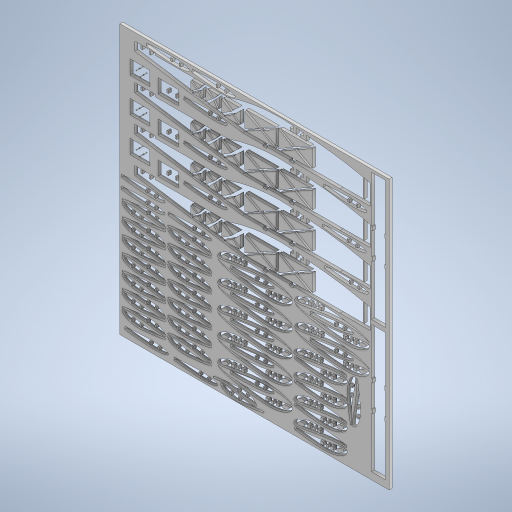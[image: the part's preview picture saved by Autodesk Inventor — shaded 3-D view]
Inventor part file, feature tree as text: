
AUTODESK INVENTOR PART (.ipt)
format: ipt  version: 2024 (Build 280153000, 153)  size: 2,372,096 bytes
history: native  units: in
note: dims shown in document units (in); Inventor stores cm internally (conversion verified against a paired STEP export)
features: extrude x13, sketch x13, pattern_linear x9
ambient origin geometry x8: Origin, YZ Plane, XZ Plane, XY Plane, X Axis, Y Axis, Z Axis, Center Point
bodies: Solid1 (feature_tree)
feature tree (35):
  extrude  "Extrusion1"  Depth=0.3937in TaperAngle=0.0deg
  extrude  "Extrusion6"  Depth=0.3937in TaperAngle=0.0deg
  pattern_linear  "Rectangular Pattern4"  Count1=3 Spacing1=4.685in
  extrude  "Extrusion7"  Depth=6.0236in
  pattern_linear  "Rectangular Pattern5"  Count1=2 Spacing1=6.0236in
  extrude  "Extrusion9"  Depth=3.0315in
  pattern_linear  "Rectangular Pattern7"  Count1=2 Spacing1=3.0315in
  extrude  "Extrusion10"  Depth=0.3937in
  pattern_linear  "Rectangular Pattern8"  Count1=5 Spacing1=2.9921in
  extrude  "Extrusion11"  Depth=0.7874in
  pattern_linear  "Rectangular Pattern9"  Count1=4  [1 undecoded]
  extrude  "Extrusion12"  Depth=0.0344in
  pattern_linear  "Rectangular Pattern10"  Spacing1=0.0197in  [1 undecoded]
  extrude  "Extrusion13"  Depth=0.0344in
  pattern_linear  "Rectangular Pattern11"  Spacing1=0.0344in  [1 undecoded]
  extrude  "Extrusion14"  [1 undecoded]
  pattern_linear  "Rectangular Pattern12"  [2 undecoded]
  extrude  "Extrusion15"  [1 undecoded]
  extrude  "Extrusion16"  [1 undecoded]
  extrude  "Extrusion17"  [1 undecoded]
  extrude  "Extrusion18"  [1 undecoded]
  pattern_linear  "Rectangular Pattern13"  [2 undecoded]
  sketch  "Sketch1"  dims[d2=0.3937in d3=0.0in d21=0.3937in d22=0.0in]
  sketch  "Sketch7"  dims[d23=1.1811in d25=4.5276in d26=0.3937in d27=0.0in d28=1.1811in d30=4.685in]
  sketch  "Sketch8"  dims[d36=0.3937in d37=0.0in d38=2.7559in d40=2.0472in d41=0.7874in d43=6.0236in]
  sketch  "Sketch10"  dims[d44=0.3937in d45=0.0in d46=1.9685in d48=3.0315in]
  sketch  "Sketch11"  dims[d49=0.3937in d50=0.0in d51=0.7874in d53=3.0315in]
  sketch  "Sketch12"  dims[d54=0.3937in d55=0.0in d56=1.5748in d58=2.6772in]
  sketch  "Sketch13"  dims[d59=0.3937in d60=0.0in d61=1.9685in d63=2.9921in]
  sketch  "Sketch14"  dims[d64=0.3937in d65=0.0in d66=0.7874in d68=3.0315in]
  sketch  "Sketch15"  dims[d69=0.3937in d70=0.0in]
  sketch  "Sketch16"  dims[d71=0.3937in d72=0.0in]
  sketch  "Sketch17"  dims[d73=0.3937in d74=0.0in]
  sketch  "Sketch18"  dims[d75=0.3937in d76=0.0in d77=1.5748in d79=4.7244in]
  sketch  "Sketch19"  dims[d31=0.0197in d32=0.0344in d33=0.0197in d34=0.0344in d39=0.0344in]
note: 12 required parameter values undecoded (feature->parameter linkage not recoverable at this tier; creation-order binding heuristic only, values carry confidence <= 0.55)
